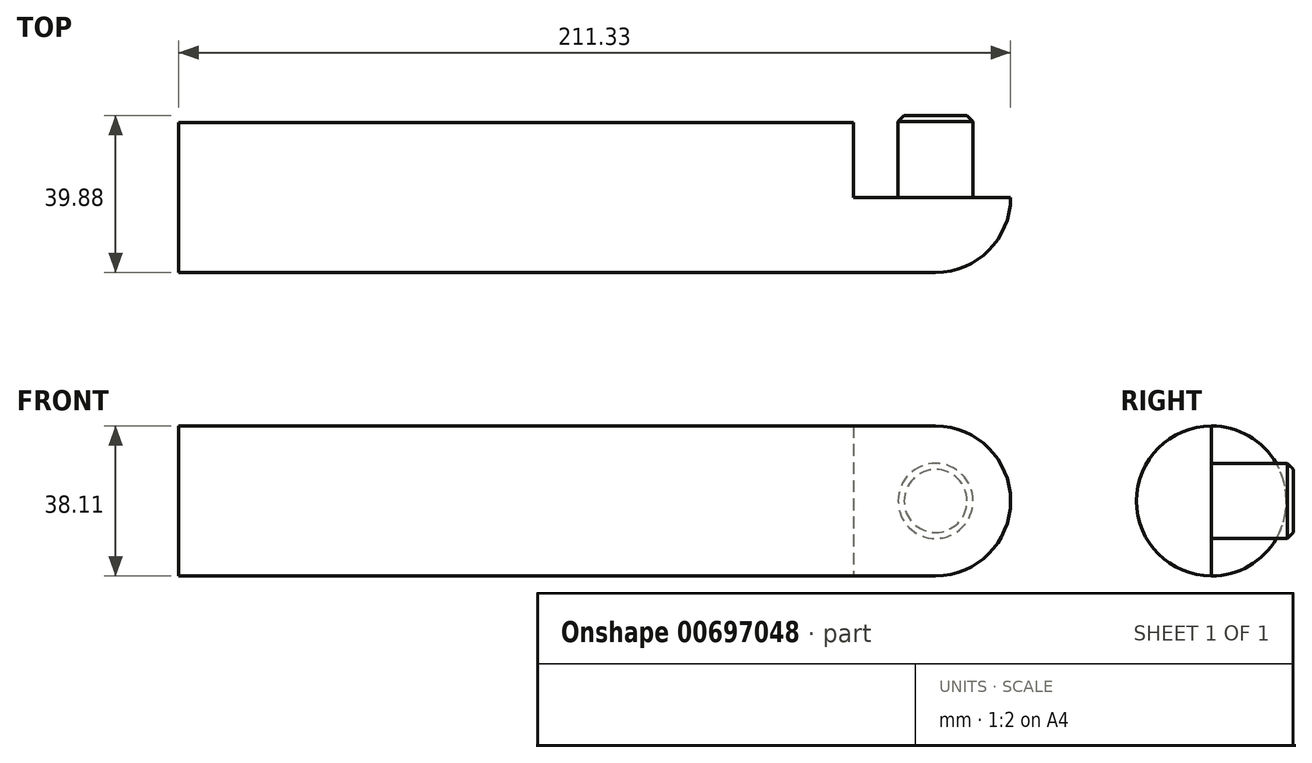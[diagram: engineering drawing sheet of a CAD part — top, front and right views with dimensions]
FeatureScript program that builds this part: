
annotation { "Feature Type Name" : "Feature", "Feature Type Description" : "" }
export const myFeature = defineFeature(function(context is Context, id is Id, definition is map)
    precondition{}
    {
        {
            var Q0;
            Q0=qCreatedBy(makeId("Front.planeOp"),FACE);
            var sketch = newSketch(context, id + "F0", { "sketchPlane" : qUnion([Q0])});
            skLineSegment(sketch, "E0.bottom", {"start": v(-85.72, -9.52) * mm, "end": v(85.72, -9.52) * mm});
            skLineSegment(sketch, "E0.top", {"start": v(-85.73, 9.52) * mm, "end": v(85.72, 9.52) * mm});
            skLineSegment(sketch, "E0.left", {"start": v(-85.73, -9.52) * mm, "end": v(-85.73, 9.52) * mm});
            skLineSegment(sketch, "E0.right", {"start": v(85.72, -9.52) * mm, "end": v(85.72, 9.52) * mm});
            skPoint(sketch, "E0.middle", {"position": v(0, 0) * mm});
            skSolve(sketch);
        }
        {
            var Q0;
            Q0=makeQuery(id+"F0.imprint","IMPRINT",FACE,{"disambiguationData":[TD([[makeQuery(id+"F0.imprint","IMPRINT",EDGE,{"derivedFrom":sQuery(id+"F0.wireOp",EDGE,"E0.bottom")}),1.0]])]});
            var Q1;
            Q1=sQuery(id+"F0.wireOp",EDGE,"E0.bottom");
            revolve(context, id + "F1", {"entities" : qUnion([Q0]), "axis" : qUnion([Q1]), "revolveType" : RevolveType.FULL});
        }
        {
            var Q0;
            Q0=makeQuery(id+"F1.opRevolve","SWEPT_FACE",FACE,{"disambiguationData":[OSD([sQuery(id+"F0.wireOp",EDGE,"E0.right")])]});
            var sketch = newSketch(context, id + "F2", { "sketchPlane" : qUnion([Q0])});
            skLineSegment(sketch, "E1", {"start": v(0, 9.52) * mm, "end": v(0, -28.57) * mm});
            skSolve(sketch);
        }
        {
            var Q0;
            Q0=qSketchRegion(id+"F2",true);
            var Q1;
            {var subQ0=sQuery(id+"F2.wireOp",EDGE,"E1");Q1=makeQuery(id+"F2.imprint","IMPRINT",FACE,{"disambiguationData":[TD([[makeQuery(id+"F2.imprint","IMPRINT",EDGE,{"derivedFrom":subQ0}),-1.0]])]});}
            extrude(context, id + "F3", {"entities" : qUnion([Q0, Q1]), "operationType" : NewBodyOperationType.ADD, "depth" : 20.83 * mm});
        }
        {
            var Q0;
            Q0=makeQuery(id+"F3.opExtrude","CAP_FACE",FACE,{"disambiguationData":[OSD([sQuery(id+"F0.wireOp",EDGE,"E0.top"),sQuery(id+"F0.wireOp",EDGE,"E0.right"),sQuery(id+"F2.wireOp",EDGE,"E1")])],"isStart":false});
            var sketch = newSketch(context, id + "F4", { "sketchPlane" : qUnion([Q0])});
            skLineSegment(sketch, "E2", {"start": v(0, -9.52) * mm, "end": v(-19.05, -9.52) * mm, "construction": true});
            skSolve(sketch);
        }
        {
            var Q0;
            Q0=qSketchRegion(id+"F4",true);
            var Q1;
            Q1=makeQuery(id+"F4.imprint","IMPRINT",FACE,{"disambiguationData":[TD([[makeQuery(id+"F4.imprint","IMPRINT",EDGE,{"derivedFrom":makeQuery(id+"F3.opExtrude","CAP_EDGE",EDGE,{"disambiguationData":[OSD([sQuery(id+"F2.wireOp",EDGE,"E1")])],"isStart":false})}),-1.0]])]});
            var Q2;
            Q2=makeQuery(id+"F3.opExtrude","CAP_EDGE",EDGE,{"disambiguationData":[OSD([sQuery(id+"F2.wireOp",EDGE,"E1")])],"isStart":false});
            revolve(context, id + "F5", {"operationType" : NewBodyOperationType.ADD, "entities" : qUnion([Q0, Q1]), "axis" : qUnion([Q2]), "revolveType" : RevolveType.ONE_DIRECTION, "oppositeDirection" : true, "angle" : 90 * degree});
        }
        {
            var Q0;
            {var subQ0=sQuery(id+"F2.wireOp",EDGE,"E1");Q0=makeQuery(id+"F5.boolean.opBoolean","MERGE",FACE,{"derivedFrom":[makeQuery(id+"F3.opExtrude","SWEPT_FACE",FACE,{"disambiguationData":[OSD([subQ0])]}),makeQuery(id+"F5.opRevolve","CAP_FACE",FACE,{"disambiguationData":[OSD([sQuery(id+"F0.wireOp",EDGE,"E0.top"),sQuery(id+"F0.wireOp",EDGE,"E0.right"),subQ0])],"isStart":false})]});}
            var sketch = newSketch(context, id + "F6", { "sketchPlane" : qUnion([Q0])});
            skLineSegment(sketch, "E3", {"start": v(-106.55, 9.52) * mm, "end": v(-106.55, -28.57) * mm, "construction": true});
            skCircle(sketch, "E4", {"center": v(-106.55, -9.52) * mm, "radius": 9.53 * mm});
            skSolve(sketch);
        }
        {
            var Q0;
            Q0=makeQuery(id+"F6.imprint","IMPRINT",FACE,{"disambiguationData":[TD([[makeQuery(id+"F6.imprint","IMPRINT",EDGE,{"derivedFrom":sQuery(id+"F6.wireOp",EDGE,"E4")}),1.0]])]});
            extrude(context, id + "F7", {"entities" : qUnion([Q0]), "operationType" : NewBodyOperationType.ADD, "depth" : 20.83 * mm});
        }
        {
            var Q0;
            Q0=makeQuery(id+"F7.opExtrude","CAP_EDGE",EDGE,{"disambiguationData":[OSD([sQuery(id+"F6.wireOp",EDGE,"E4")])],"isStart":false});
            chamfer(context, id + "F8", {"entities" : qUnion([Q0]), "width" : 1.52 * mm, "tangentPropagation" : true});
        }
    });
